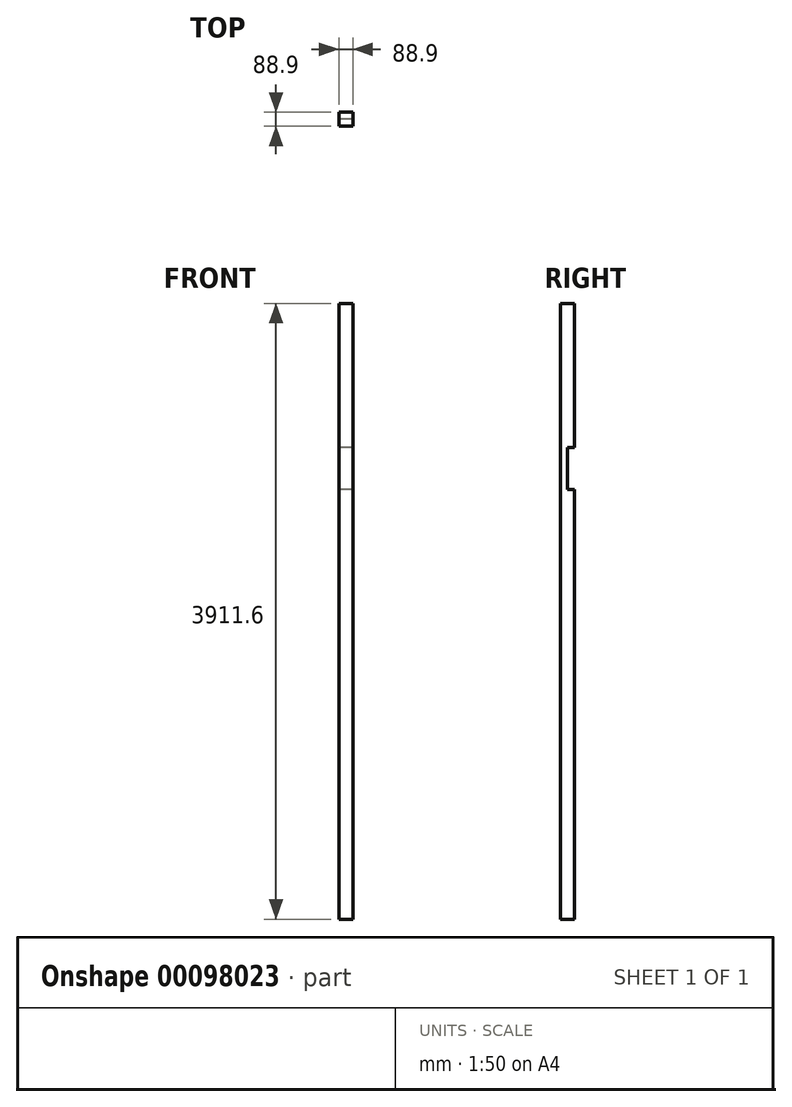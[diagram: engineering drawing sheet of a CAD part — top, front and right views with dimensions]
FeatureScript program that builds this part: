
annotation { "Feature Type Name" : "Feature", "Feature Type Description" : "" }
export const myFeature = defineFeature(function(context is Context, id is Id, definition is map)
    precondition{}
    {
        {
            var Q0;
            Q0=qCreatedBy(makeId("Front.planeOp"),FACE);
            var sketch = newSketch(context, id + "F0", { "sketchPlane" : qUnion([Q0])});
            skLineSegment(sketch, "E0.bottom", {"start": v(-44.45, 1955.8) * mm, "end": v(44.45, 1955.8) * mm});
            skLineSegment(sketch, "E0.top", {"start": v(-44.45, -1955.8) * mm, "end": v(44.45, -1955.8) * mm});
            skLineSegment(sketch, "E0.left", {"start": v(-44.45, 1955.8) * mm, "end": v(-44.45, -1955.8) * mm});
            skLineSegment(sketch, "E0.right", {"start": v(44.45, 1955.8) * mm, "end": v(44.45, -1955.8) * mm});
            skPoint(sketch, "E0.middle", {"position": v(0, 0) * mm});
            skSolve(sketch);
        }
        {
            var Q0;
            Q0 = qSketchRegion(id + "F0", true);
            extrude(context, id + "F1", {"entities" : qUnion([Q0]), "depth" : 88.9 * mm});
        }
        {
            var Q0;
            Q0=makeQuery(id+"F1.opExtrude","SWEPT_FACE",FACE,{"disambiguationData":[OSD([sQuery(id+"F0.wireOp",EDGE,"E0.left")])]});
            var sketch = newSketch(context, id + "F2", { "sketchPlane" : qUnion([Q0])});
            skLineSegment(sketch, "E1", {"start": v(0, 1041.4) * mm, "end": v(44.45, 1041.4) * mm});
            skLineSegment(sketch, "E2", {"start": v(44.45, 1041.4) * mm, "end": v(44.45, 774.7) * mm});
            skLineSegment(sketch, "E3", {"start": v(44.45, 774.7) * mm, "end": v(0, 774.7) * mm});
            skLineSegment(sketch, "E4", {"start": v(0, 774.7) * mm, "end": v(0, 1041.4) * mm});
            skSolve(sketch);
        }
        {
            var Q0;
            Q0 = qSketchRegion(id + "F2", true);
            extrude(context, id + "F3", {"entities" : qUnion([Q0]), "operationType" : NewBodyOperationType.REMOVE, "endBound" : BoundingType.THROUGH_ALL, "oppositeDirection" : true, "depth" : 25.4 * mm});
        }
    });
